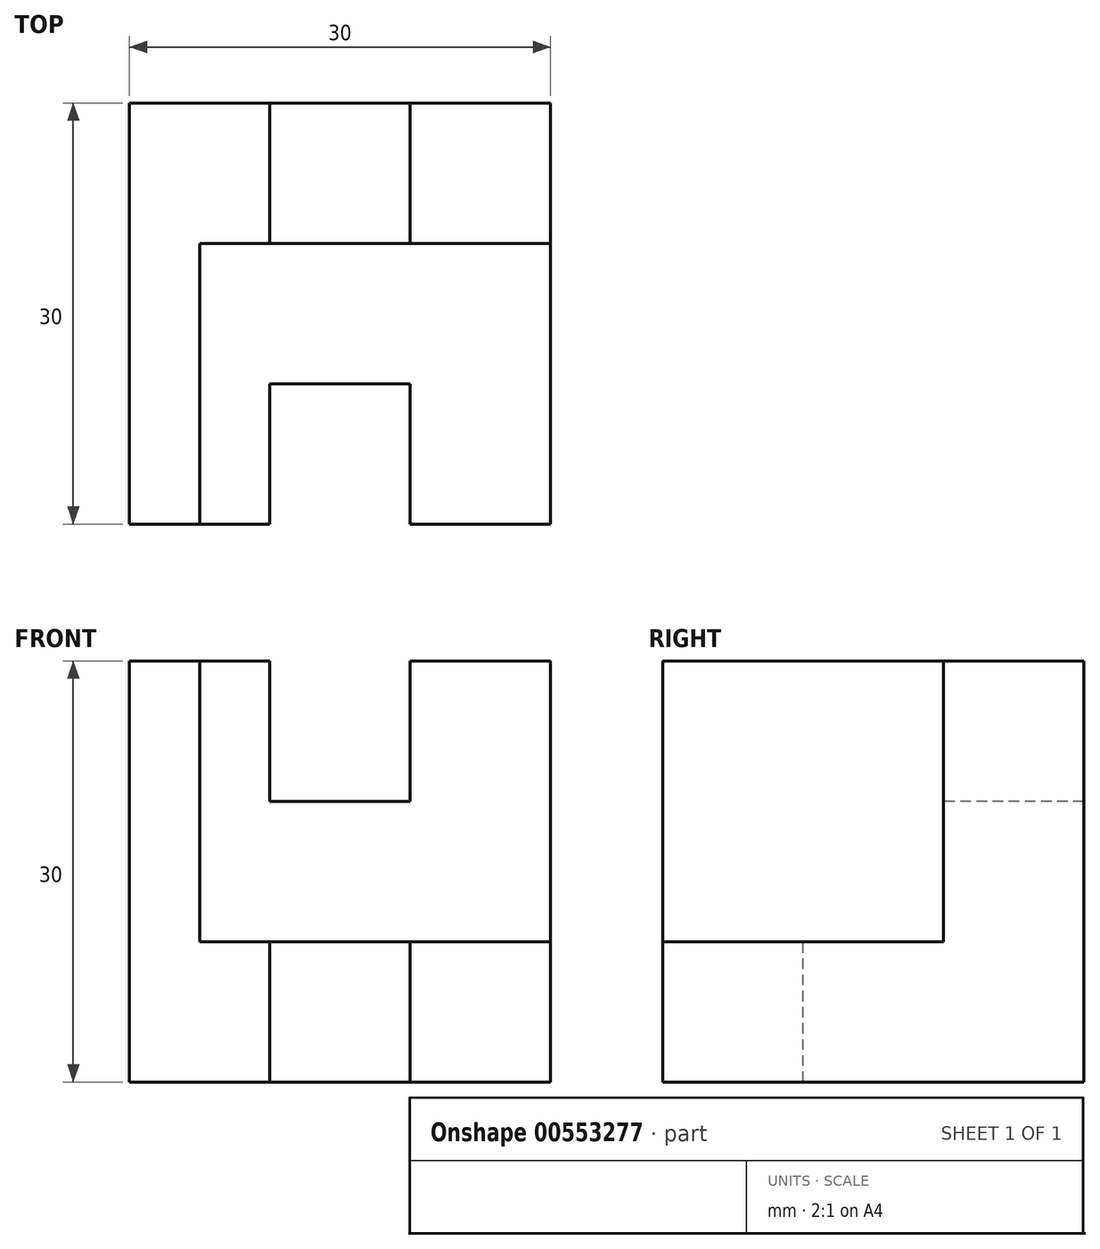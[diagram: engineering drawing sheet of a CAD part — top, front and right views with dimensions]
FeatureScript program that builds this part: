
annotation { "Feature Type Name" : "Feature", "Feature Type Description" : "" }
export const myFeature = defineFeature(function(context is Context, id is Id, definition is map)
    precondition{}
    {
        {
            var Q0;
            Q0=qCreatedBy(makeId("Top.planeOp"),FACE);
            var sketch = newSketch(context, id + "F0", { "sketchPlane" : qUnion([Q0])});
            skLineSegment(sketch, "E0.bottom", {"start": v(0, 0) * mm, "end": v(30, 0) * mm});
            skLineSegment(sketch, "E0.top", {"start": v(0, 30) * mm, "end": v(30, 30) * mm});
            skLineSegment(sketch, "E0.left", {"start": v(0, 0) * mm, "end": v(0, 30) * mm});
            skLineSegment(sketch, "E0.right", {"start": v(30, 0) * mm, "end": v(30, 30) * mm});
            skSolve(sketch);
        }
        {
            var Q0;
            Q0=qSketchRegion(id+"F0",true);
            extrude(context, id + "F1", {"entities" : qUnion([Q0]), "depth" : 30 * mm, "offsetDistance" : 25 * mm});
        }
        {
            var Q0;
            Q0=makeQuery(id+"F1.opExtrude","SWEPT_FACE",FACE,{"disambiguationData":[OSD([sQuery(id+"F0.wireOp",EDGE,"E0.bottom")])]});
            var sketch = newSketch(context, id + "F2", { "sketchPlane" : qUnion([Q0])});
            skLineSegment(sketch, "E1.bottom", {"start": v(30, 30) * mm, "end": v(5, 30) * mm});
            skLineSegment(sketch, "E1.top", {"start": v(30, 10) * mm, "end": v(5, 10) * mm});
            skLineSegment(sketch, "E1.left", {"start": v(30, 30) * mm, "end": v(30, 10) * mm});
            skLineSegment(sketch, "E1.right", {"start": v(5, 30) * mm, "end": v(5, 10) * mm});
            skSolve(sketch);
        }
        {
            var Q0;
            Q0 = qSketchRegion(id + "F2", true);
            extrude(context, id + "F3", {"entities" : qUnion([Q0]), "operationType" : NewBodyOperationType.REMOVE, "oppositeDirection" : true, "depth" : 20 * mm, "offsetDistance" : 25 * mm});
        }
        {
            var Q0;
            Q0=makeQuery(id+"F3.boolean.opBoolean","COPY",FACE,{"derivedFrom":makeQuery(id+"F3.opExtrude","CAP_FACE",FACE,{"disambiguationData":[OSD([sQuery(id+"F2.wireOp",EDGE,"E1.bottom"),sQuery(id+"F2.wireOp",EDGE,"E1.top"),sQuery(id+"F2.wireOp",EDGE,"E1.left"),sQuery(id+"F2.wireOp",EDGE,"E1.right")])],"isStart":false})});
            var sketch = newSketch(context, id + "F4", { "sketchPlane" : qUnion([Q0])});
            skLineSegment(sketch, "E2.bottom", {"start": v(20, 30) * mm, "end": v(10, 30) * mm});
            skLineSegment(sketch, "E2.top", {"start": v(20, 20) * mm, "end": v(10, 20) * mm});
            skLineSegment(sketch, "E2.left", {"start": v(20, 30) * mm, "end": v(20, 20) * mm});
            skLineSegment(sketch, "E2.right", {"start": v(10, 30) * mm, "end": v(10, 20) * mm});
            skSolve(sketch);
        }
        {
            var Q0;
            Q0 = qSketchRegion(id + "F4", true);
            extrude(context, id + "F5", {"entities" : qUnion([Q0]), "operationType" : NewBodyOperationType.REMOVE, "endBound" : BoundingType.THROUGH_ALL, "oppositeDirection" : true, "depth" : 25 * mm, "offsetDistance" : 25 * mm});
        }
        {
            var Q0;
            Q0=makeQuery(id+"F3.boolean.opBoolean","COPY",FACE,{"derivedFrom":makeQuery(id+"F3.opExtrude","SWEPT_FACE",FACE,{"disambiguationData":[OSD([sQuery(id+"F2.wireOp",EDGE,"E1.top")])]})});
            var sketch = newSketch(context, id + "F6", { "sketchPlane" : qUnion([Q0])});
            skLineSegment(sketch, "E3.bottom", {"start": v(20, 0) * mm, "end": v(10, 0) * mm});
            skLineSegment(sketch, "E3.top", {"start": v(20, 10) * mm, "end": v(10, 10) * mm});
            skLineSegment(sketch, "E3.left", {"start": v(20, 0) * mm, "end": v(20, 10) * mm});
            skLineSegment(sketch, "E3.right", {"start": v(10, 0) * mm, "end": v(10, 10) * mm});
            skSolve(sketch);
        }
        {
            var Q0;
            Q0 = qSketchRegion(id + "F6", true);
            extrude(context, id + "F7", {"entities" : qUnion([Q0]), "operationType" : NewBodyOperationType.REMOVE, "endBound" : BoundingType.THROUGH_ALL, "oppositeDirection" : true, "depth" : 25 * mm, "offsetDistance" : 25 * mm});
        }
    });
